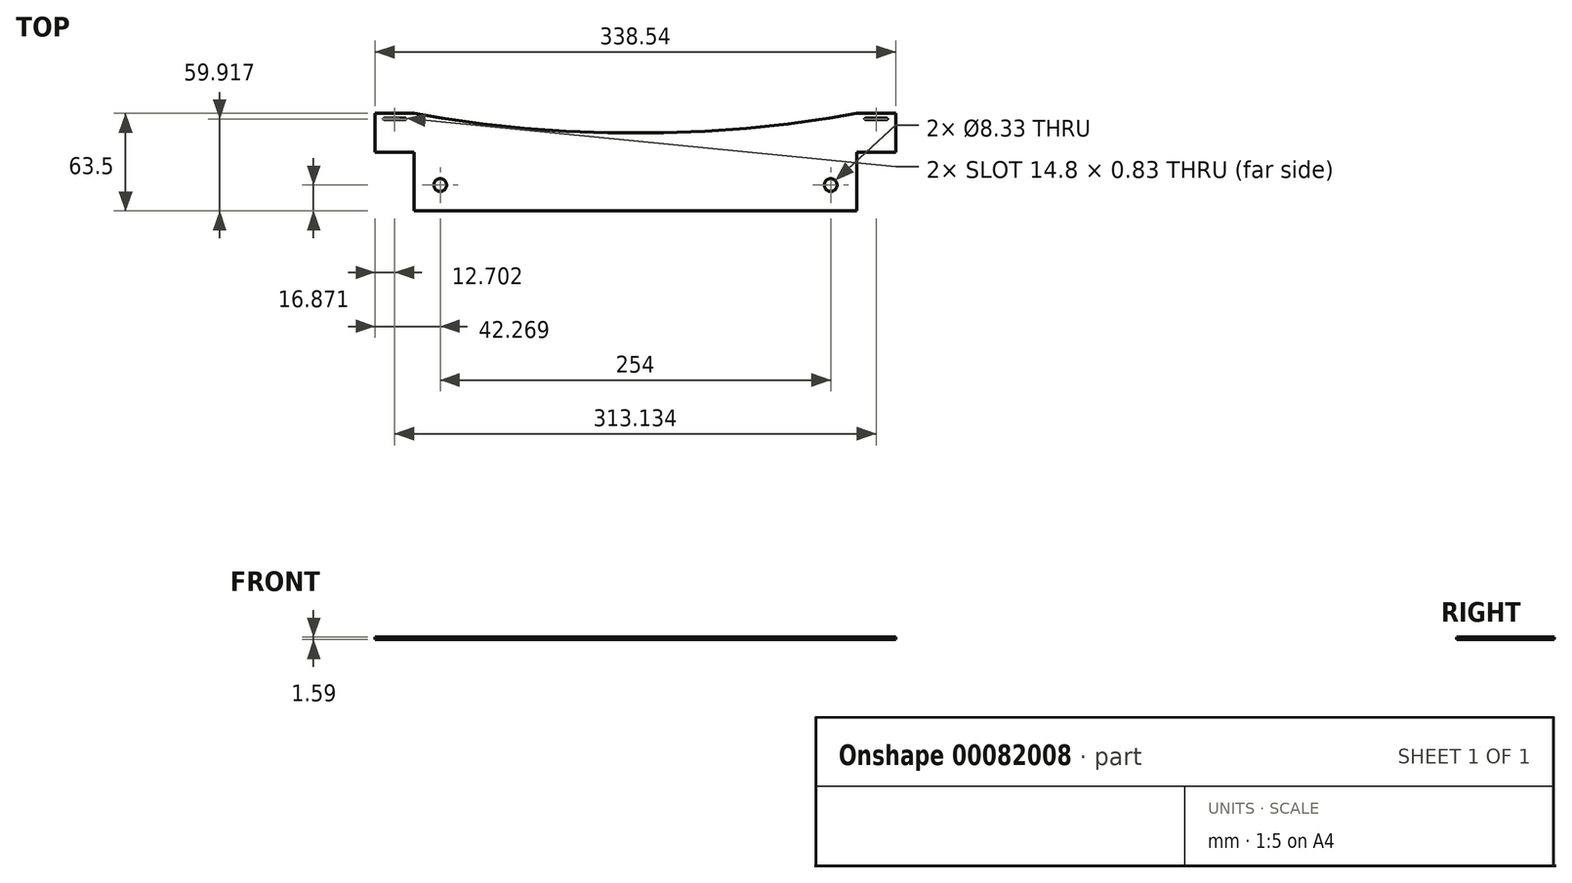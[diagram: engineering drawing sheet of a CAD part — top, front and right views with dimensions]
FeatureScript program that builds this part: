
annotation { "Feature Type Name" : "Feature", "Feature Type Description" : "" }
export const myFeature = defineFeature(function(context is Context, id is Id, definition is map)
    precondition{}
    {
        {
            var Q0;
            Q0=qCreatedBy(makeId("Top.planeOp"),FACE);
            var sketch = newSketch(context, id + "F0", { "sketchPlane" : qUnion([Q0])});
            skLineSegment(sketch, "E0", {"start": v(-244.03, 13.53) * mm, "end": v(-218.63, 13.53) * mm});
            skArc(sketch, "E1", {"start": v(-218.63, 13.53) * mm, "mid": v(-147, 3.77) * mm, "end": v(-74.76, 0.83) * mm});
            skLineSegment(sketch, "E2", {"start": v(-218.63, 13.53) * mm, "end": v(-218.63, -11.87) * mm, "construction": true});
            skArc(sketch, "E3", {"start": v(-238.31, 10.36) * mm, "mid": v(-238.73, 9.95) * mm, "end": v(-238.31, 9.53) * mm});
            skArc(sketch, "E4.MirrorC", {"start": v(-224.34, 10.36) * mm, "mid": v(-223.93, 9.95) * mm, "end": v(-224.34, 9.53) * mm});
            skLineSegment(sketch, "E5", {"start": v(-238.31, 10.36) * mm, "end": v(-224.34, 10.36) * mm});
            skLineSegment(sketch, "E6", {"start": v(-224.34, 9.53) * mm, "end": v(-238.31, 9.53) * mm});
            skLineSegment(sketch, "E7", {"start": v(-244.03, 13.53) * mm, "end": v(-244.03, -11.87) * mm});
            skLineSegment(sketch, "E8", {"start": v(-218.63, -49.97) * mm, "end": v(-74.76, -49.97) * mm});
            skLineSegment(sketch, "E9", {"start": v(-218.63, -11.87) * mm, "end": v(-244.03, -11.87) * mm});
            skLineSegment(sketch, "E10", {"start": v(-74.76, -49.97) * mm, "end": v(-74.76, -11.87) * mm});
            skLineSegment(sketch, "E11", {"start": v(-218.63, -11.87) * mm, "end": v(-218.63, -49.97) * mm});
            skLineSegment(sketch, "E12", {"start": v(-74.76, 34.74) * mm, "end": v(-74.76, -80.38) * mm, "construction": true});
            skLineSegment(sketch, "E13", {"start": v(-74.76, -11.87) * mm, "end": v(-218.63, -11.87) * mm, "construction": true});
            skLineSegment(sketch, "E14.0", {"start": v(-205.93, -37.27) * mm, "end": v(-86.55, -37.27) * mm, "construction": true});
            skLineSegment(sketch, "E14.1", {"start": v(-205.93, -6.79) * mm, "end": v(-205.93, -37.27) * mm, "construction": true});
            skCircle(sketch, "E15", {"center": v(-201.76, -33.1) * mm, "radius": 4.17 * mm});
            skLineSegment(sketch, "E16.MirrorCS", {"start": v(-74.76, -11.87) * mm, "end": v(69.1, -11.87) * mm, "construction": true});
            skLineSegment(sketch, "E17.MirrorCS", {"start": v(56.4, -37.27) * mm, "end": v(-62.97, -37.27) * mm, "construction": true});
            skArc(sketch, "E18.MirrorCS", {"start": v(69.1, 13.53) * mm, "mid": v(-2.53, 3.77) * mm, "end": v(-74.76, 0.83) * mm});
            skLineSegment(sketch, "E19.MirrorCS", {"start": v(69.1, -49.97) * mm, "end": v(-74.76, -49.97) * mm});
            skArc(sketch, "E20.MirrorCS", {"start": v(74.82, 10.36) * mm, "mid": v(74.4, 9.95) * mm, "end": v(74.82, 9.53) * mm});
            skArc(sketch, "E21.MirrorCS", {"start": v(88.8, 10.36) * mm, "mid": v(89.2, 9.95) * mm, "end": v(88.8, 9.53) * mm});
            skLineSegment(sketch, "E22.MirrorCS", {"start": v(56.4, -6.79) * mm, "end": v(56.4, -37.27) * mm, "construction": true});
            skLineSegment(sketch, "E23.MirrorCS", {"start": v(69.1, 13.53) * mm, "end": v(69.1, -11.87) * mm, "construction": true});
            skCircle(sketch, "E24.MirrorC", {"center": v(52.24, -33.1) * mm, "radius": 4.17 * mm});
            skLineSegment(sketch, "E25.MirrorCS", {"start": v(69.1, -11.87) * mm, "end": v(69.1, -49.97) * mm});
            skLineSegment(sketch, "E26.MirrorCS", {"start": v(69.1, -11.87) * mm, "end": v(94.5, -11.87) * mm});
            skLineSegment(sketch, "E27.MirrorCS", {"start": v(74.82, 9.53) * mm, "end": v(88.8, 9.53) * mm});
            skLineSegment(sketch, "E28.MirrorCS", {"start": v(88.8, 10.36) * mm, "end": v(74.82, 10.36) * mm});
            skLineSegment(sketch, "E29.MirrorCS", {"start": v(94.5, 13.53) * mm, "end": v(94.5, -11.87) * mm});
            skLineSegment(sketch, "E30.MirrorCS", {"start": v(94.5, 13.53) * mm, "end": v(69.1, 13.53) * mm});
            skSolve(sketch);
        }
        {
            var Q0;
            Q0 = qSketchRegion(id + "F0", true);
            extrude(context, id + "F1", {"entities" : qUnion([Q0]), "depth" : 1.59 * mm});
        }
    });
